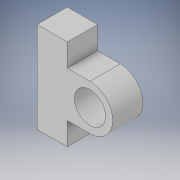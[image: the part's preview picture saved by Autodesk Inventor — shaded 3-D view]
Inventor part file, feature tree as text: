
AUTODESK INVENTOR PART (.ipt)
format: ipt  version: 2018 (Build 220112000, 112)  size: 115,200 bytes
history: native  units: mm
features: extrude x1, sketch x1
ambient origin geometry x8: Origin, YZ Plane, XZ Plane, XY Plane, X Axis, Y Axis, Z Axis, Center Point
bodies: Volumenkörper1 (feature_tree)
feature tree (2):
  extrude  "Extrusion1"  Depth=15.0mm
  sketch  "Skizze1"  dims[d0=30.0mm d1=15.0mm d2=10.3mm d3=15.0mm d7=10.0mm d8=17.5mm d12=10.0mm d13=0.0mm d14=7.5mm d15=7.5mm d16=1.8mm d17=1.8mm]
